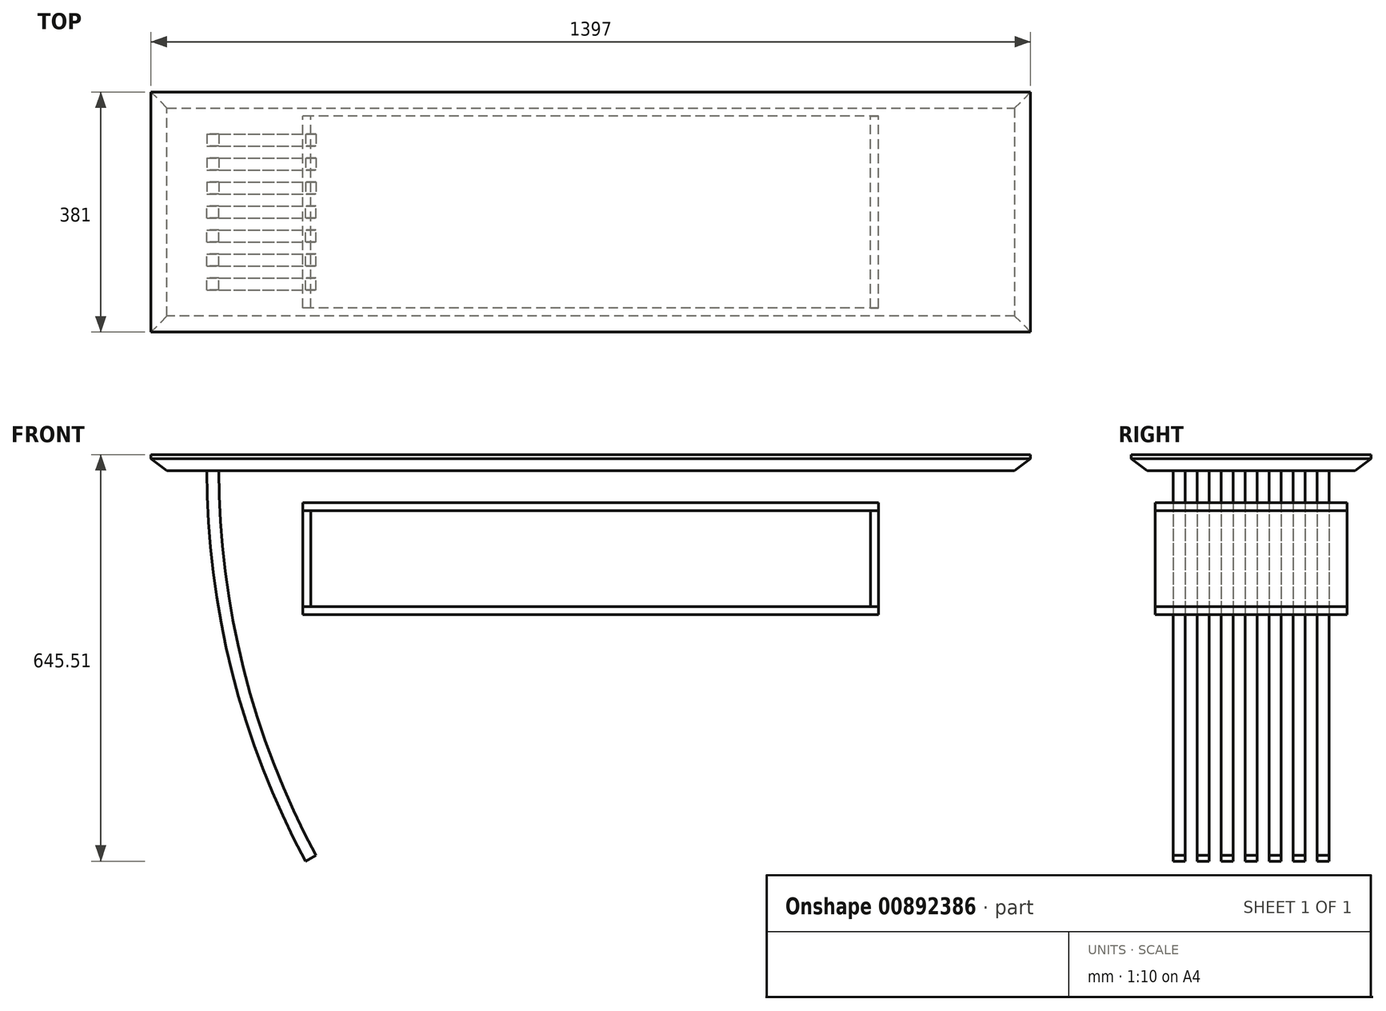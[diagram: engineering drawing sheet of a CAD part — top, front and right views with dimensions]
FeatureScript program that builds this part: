
annotation { "Feature Type Name" : "Feature", "Feature Type Description" : "" }
export const myFeature = defineFeature(function(context is Context, id is Id, definition is map)
    precondition{}
    {
        {
            var Q0;
            Q0=qCreatedBy(makeId("Front.planeOp"),FACE);
            var sketch = newSketch(context, id + "F0", { "sketchPlane" : qUnion([Q0])});
            skLineSegment(sketch, "E0.bottom", {"start": v(698.5, -12.7) * mm, "end": v(-698.5, -12.7) * mm});
            skLineSegment(sketch, "E0.top", {"start": v(698.5, 12.7) * mm, "end": v(-698.5, 12.7) * mm});
            skLineSegment(sketch, "E0.left", {"start": v(698.5, -12.7) * mm, "end": v(698.5, 12.7) * mm});
            skLineSegment(sketch, "E0.right", {"start": v(-698.5, -12.7) * mm, "end": v(-698.5, 12.7) * mm});
            skPoint(sketch, "E0.middle", {"position": v(0, 0) * mm});
            skLineSegment(sketch, "E1.bottom", {"start": v(457.2, -63.5) * mm, "end": v(-457.2, -63.5) * mm});
            skLineSegment(sketch, "E1.top", {"start": v(457.2, -241.3) * mm, "end": v(-457.2, -241.3) * mm});
            skLineSegment(sketch, "E1.left", {"start": v(457.2, -63.5) * mm, "end": v(457.2, -241.3) * mm});
            skLineSegment(sketch, "E1.right", {"start": v(-457.2, -63.5) * mm, "end": v(-457.2, -241.3) * mm});
            skPoint(sketch, "E1.middle", {"position": v(0, -152.4) * mm});
            skLineSegment(sketch, "E2.0", {"start": v(444.5, -76.2) * mm, "end": v(-444.5, -76.2) * mm});
            skLineSegment(sketch, "E2.1", {"start": v(444.5, -76.2) * mm, "end": v(444.5, -228.6) * mm});
            skLineSegment(sketch, "E2.2", {"start": v(444.5, -228.6) * mm, "end": v(-444.5, -228.6) * mm});
            skLineSegment(sketch, "E2.3", {"start": v(-444.5, -76.2) * mm, "end": v(-444.5, -228.6) * mm});
            skLineSegment(sketch, "E3", {"start": v(-444.5, -76.2) * mm, "end": v(-457.2, -76.2) * mm});
            skLineSegment(sketch, "E4", {"start": v(-444.5, -228.6) * mm, "end": v(-457.2, -228.6) * mm});
            skLineSegment(sketch, "E5", {"start": v(444.5, -228.6) * mm, "end": v(457.2, -228.6) * mm});
            skLineSegment(sketch, "E6", {"start": v(444.5, -76.2) * mm, "end": v(457.2, -76.2) * mm});
            skArc(sketch, "E7", {"start": v(-609.6, -12.7) * mm, "mid": v(-569.92, -332.46) * mm, "end": v(-453.27, -632.81) * mm});
            skArc(sketch, "E8", {"start": v(571.5, -698.5) * mm, "mid": v(0, -530.7) * mm, "end": v(-571.5, -698.5) * mm});
            skArc(sketch, "E9.0", {"start": v(594.66, -698.5) * mm, "mid": v(0, -518) * mm, "end": v(-594.66, -698.5) * mm});
            skLineSegment(sketch, "E10", {"start": v(-594.66, -698.5) * mm, "end": v(-571.5, -698.5) * mm});
            skLineSegment(sketch, "E11", {"start": v(594.66, -698.5) * mm, "end": v(571.5, -698.5) * mm});
            skPoint(sketch, "E12.orphan", {"position": v(-415.41, -698.5) * mm});
            skSolve(sketch);
        }
        {
            var Q0;
            Q0=makeQuery(id+"F0.imprint","IMPRINT",FACE,{"disambiguationData":[TD([[makeQuery(id+"F0.imprint","IMPRINT",EDGE,{"derivedFrom":sQuery(id+"F0.wireOp",EDGE,"E0.top")}),1.0]])]});
            extrude(context, id + "F1", {"entities" : qUnion([Q0]), "endBound" : BoundingType.SYMMETRIC, "depth" : 381 * mm, "offsetDistance" : 25.4 * mm});
        }
        {
            var Q0;
            Q0=makeQuery(id+"F0.imprint","IMPRINT",FACE,{"disambiguationData":[TD([[makeQuery(id+"F0.imprint","IMPRINT",EDGE,{"derivedFrom":sQuery(id+"F0.wireOp",EDGE,"E2.3")}),-1.0]])]});
            var Q1;
            Q1=makeQuery(id+"F0.imprint","IMPRINT",FACE,{"disambiguationData":[TD([[makeQuery(id+"F0.imprint","IMPRINT",EDGE,{"derivedFrom":sQuery(id+"F0.wireOp",EDGE,"E2.1")}),1.0]])]});
            extrude(context, id + "F2", {"entities" : qUnion([Q0, Q1]), "endBound" : BoundingType.SYMMETRIC, "depth" : 304.8 * mm, "offsetDistance" : 25.4 * mm});
        }
        {
            var Q0;
            {var subQ1=sQuery(id+"F0.wireOp",EDGE,"E1.bottom");Q0=makeQuery(id+"F0.imprint","IMPRINT",FACE,{"disambiguationData":[TD([[makeQuery(id+"F0.imprint","IMPRINT",EDGE,{"derivedFrom":subQ1}),1.0]])]});}
            var Q1;
            {var subQ1=sQuery(id+"F0.wireOp",EDGE,"E1.top");Q1=makeQuery(id+"F0.imprint","IMPRINT",FACE,{"disambiguationData":[TD([[makeQuery(id+"F0.imprint","IMPRINT",EDGE,{"derivedFrom":subQ1}),-1.0]])]});}
            extrude(context, id + "F3", {"entities" : qUnion([Q0, Q1]), "endBound" : BoundingType.SYMMETRIC, "depth" : 304.8 * mm, "offsetDistance" : 25.4 * mm});
        }
        {
            var Q0;
            Q0=makeQuery(id+"F1.opExtrude","SWEPT_EDGE",EDGE,{"disambiguationData":[OSD([sQuery(id+"F0.wireOp",EDGE,"E0.bottom"),sQuery(id+"F0.wireOp",EDGE,"E0.right")])]});
            var Q1;
            Q1=makeQuery(id+"F1.opExtrude","CAP_EDGE",EDGE,{"disambiguationData":[OSD([sQuery(id+"F0.wireOp",EDGE,"E0.bottom")])],"isStart":false});
            var Q2;
            Q2=makeQuery(id+"F1.opExtrude","CAP_EDGE",EDGE,{"disambiguationData":[OSD([sQuery(id+"F0.wireOp",EDGE,"E0.bottom")])],"isStart":true});
            var Q3;
            Q3=makeQuery(id+"F1.opExtrude","SWEPT_EDGE",EDGE,{"disambiguationData":[OSD([sQuery(id+"F0.wireOp",EDGE,"E0.bottom"),sQuery(id+"F0.wireOp",EDGE,"E0.left")])]});
            chamfer(context, id + "F4", {"entities" : qUnion([Q0, Q1, Q2, Q3]), "chamferType" : ChamferType.TWO_OFFSETS, "width1" : 25.4 * mm, "oppositeDirection" : false, "width2" : 19.05 * mm, "tangentPropagation" : true});
        }
        {
            var Q0;
            Q0=makeQuery(id+"F1.opExtrude","SWEPT_FACE",FACE,{"disambiguationData":[OSD([sQuery(id+"F0.wireOp",EDGE,"E0.bottom")])]});
            var sketch = newSketch(context, id + "F5", { "sketchPlane" : qUnion([Q0])});
            skLineSegment(sketch, "E13.bottom", {"start": v(-590.55, 9.53) * mm, "end": v(-609.6, 9.53) * mm});
            skLineSegment(sketch, "E13.top", {"start": v(-590.55, -9.52) * mm, "end": v(-609.6, -9.52) * mm});
            skLineSegment(sketch, "E13.left", {"start": v(-590.55, 9.53) * mm, "end": v(-590.55, -9.52) * mm});
            skLineSegment(sketch, "E13.right", {"start": v(-609.6, 9.53) * mm, "end": v(-609.6, -9.52) * mm});
            skPoint(sketch, "E13.middle", {"position": v(-600.08, 0) * mm});
            skLineSegment(sketch, "E14.bottom", {"start": v(-590.55, 47.63) * mm, "end": v(-609.6, 47.63) * mm});
            skLineSegment(sketch, "E14.top", {"start": v(-590.55, 28.58) * mm, "end": v(-609.6, 28.58) * mm});
            skLineSegment(sketch, "E14.left", {"start": v(-590.55, 47.63) * mm, "end": v(-590.55, 24.77) * mm});
            skLineSegment(sketch, "E14.right", {"start": v(-609.6, 47.62) * mm, "end": v(-609.6, 28.58) * mm});
            skPoint(sketch, "E14.middle", {"position": v(-600.08, 38.1) * mm});
            skPoint(sketch, "E14.middle.positionSnap0", {"position": v(-600.08, 9.53) * mm});
            skPoint(sketch, "E14.centerSnap0", {"position": v(-600.08, 9.53) * mm});
            skLineSegment(sketch, "E15.bottom", {"start": v(-590.55, 85.73) * mm, "end": v(-609.6, 85.73) * mm});
            skLineSegment(sketch, "E15.top", {"start": v(-590.55, 66.68) * mm, "end": v(-609.6, 66.68) * mm});
            skLineSegment(sketch, "E15.left", {"start": v(-590.55, 85.73) * mm, "end": v(-590.55, 66.68) * mm});
            skLineSegment(sketch, "E15.right", {"start": v(-609.6, 85.73) * mm, "end": v(-609.6, 66.68) * mm});
            skPoint(sketch, "E15.middle", {"position": v(-600.08, 76.2) * mm});
            skLineSegment(sketch, "E16.bottom", {"start": v(-590.55, 123.83) * mm, "end": v(-609.6, 123.82) * mm});
            skLineSegment(sketch, "E16.top", {"start": v(-590.55, 104.78) * mm, "end": v(-609.6, 104.77) * mm});
            skLineSegment(sketch, "E16.left", {"start": v(-590.55, 123.83) * mm, "end": v(-590.55, 104.78) * mm});
            skLineSegment(sketch, "E16.right", {"start": v(-609.6, 123.82) * mm, "end": v(-609.6, 104.77) * mm});
            skPoint(sketch, "E16.middle", {"position": v(-600.08, 114.3) * mm});
            skLineSegment(sketch, "E17.MirrorCS", {"start": v(-609.6, -123.82) * mm, "end": v(-609.6, -104.77) * mm});
            skLineSegment(sketch, "E18.MirrorCS", {"start": v(-609.6, -85.73) * mm, "end": v(-609.6, -66.68) * mm});
            skLineSegment(sketch, "E19.MirrorCS", {"start": v(-590.55, -47.63) * mm, "end": v(-590.55, -24.77) * mm});
            skLineSegment(sketch, "E20.MirrorCS", {"start": v(-609.6, -47.62) * mm, "end": v(-609.6, -28.58) * mm});
            skLineSegment(sketch, "E21.MirrorCS", {"start": v(-590.55, -123.83) * mm, "end": v(-590.55, -104.78) * mm});
            skLineSegment(sketch, "E22.MirrorCS", {"start": v(-590.55, -85.73) * mm, "end": v(-590.55, -66.68) * mm});
            skLineSegment(sketch, "E23.MirrorCS", {"start": v(-590.55, -104.78) * mm, "end": v(-609.6, -104.78) * mm});
            skLineSegment(sketch, "E24.MirrorCS", {"start": v(-590.55, -66.68) * mm, "end": v(-609.6, -66.68) * mm});
            skLineSegment(sketch, "E25.MirrorCS", {"start": v(-590.55, -28.58) * mm, "end": v(-609.6, -28.58) * mm});
            skLineSegment(sketch, "E26.MirrorCS", {"start": v(-590.55, -47.63) * mm, "end": v(-609.6, -47.63) * mm});
            skLineSegment(sketch, "E27.MirrorCS", {"start": v(-590.55, -85.73) * mm, "end": v(-609.6, -85.73) * mm});
            skLineSegment(sketch, "E28.MirrorCS", {"start": v(-590.55, -123.83) * mm, "end": v(-609.6, -123.83) * mm});
            skPoint(sketch, "E29.MirrorP", {"position": v(-600.08, -76.2) * mm});
            skPoint(sketch, "E30.MirrorP", {"position": v(-600.08, -38.1) * mm});
            skPoint(sketch, "E31.MirrorP", {"position": v(-600.08, -114.3) * mm});
            skSolve(sketch);
        }
        {
            var Q0;
            Q0 = qSketchRegion(id + "F5", true);
            var Q1;
            Q1=sQuery(id+"F0.wireOp",EDGE,"E7");
            sweep(context, id + "F6", {"profiles" : qUnion([Q0]), "path" : qUnion([Q1])});
        }
    });
